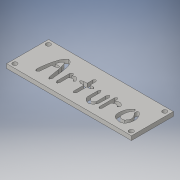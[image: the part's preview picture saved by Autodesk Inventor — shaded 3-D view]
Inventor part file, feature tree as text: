
AUTODESK INVENTOR PART (.ipt)
format: ipt  version: 2016 (Build 200138000, 138)  size: 264,192 bytes
history: native  units: mm
features: sheet_metal_op x1, sketch x1, other x1
ambient origin geometry x8: Origin, YZ Plane, XZ Plane, XY Plane, X Axis, Y Axis, Z Axis, Center Point
bodies: Body1 (feature_tree)
feature tree (3):
  sheet_metal_op  "Face5"
  sketch  "Sketch2"  dims[d0=100.800901mm d1=300.110264mm d3=10.836576mm d4=10.836576mm d5=10.836576mm d6=10.836576mm d18=10.0mm d24=10.0mm d25=10.0mm d26=7.687053mm d27=8.541mm d28=8.327641mm d29=7.259994mm d30=7.474mm d31=6.832936mm d32=7.259994mm d33=8.327641mm d34=6.832936mm d37=10.0mm]
  other  "Plate5"
